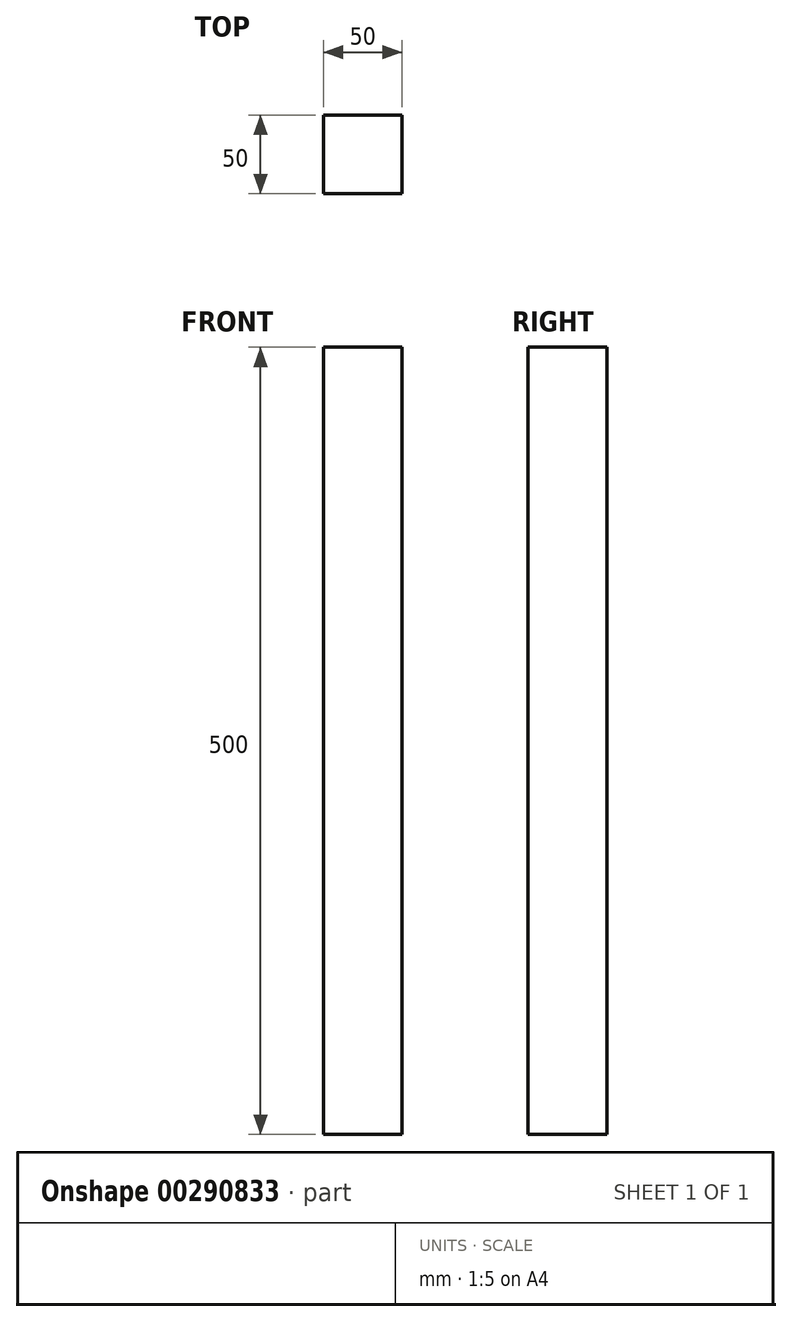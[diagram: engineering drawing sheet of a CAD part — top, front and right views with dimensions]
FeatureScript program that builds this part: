
annotation { "Feature Type Name" : "Feature", "Feature Type Description" : "" }
export const myFeature = defineFeature(function(context is Context, id is Id, definition is map)
    precondition{}
    {
        {
            var Q0;
            Q0=qCreatedBy(makeId("Top.planeOp"),FACE);
            var sketch = newSketch(context, id + "F0", { "sketchPlane" : qUnion([Q0])});
            skLineSegment(sketch, "E0.bottom", {"start": v(25, -25) * mm, "end": v(-25, -25) * mm});
            skLineSegment(sketch, "E0.top", {"start": v(25, 25) * mm, "end": v(-25, 25) * mm});
            skLineSegment(sketch, "E0.left", {"start": v(25, -25) * mm, "end": v(25, 25) * mm});
            skLineSegment(sketch, "E0.right", {"start": v(-25, -25) * mm, "end": v(-25, 25) * mm});
            skPoint(sketch, "E0.middle", {"position": v(0, 0) * mm});
            skSolve(sketch);
        }
        {
            var Q0;
            Q0=makeQuery(id+"F0.imprint","IMPRINT",FACE,{"disambiguationData":[TD([[makeQuery(id+"F0.imprint","IMPRINT",EDGE,{"derivedFrom":sQuery(id+"F0.wireOp",EDGE,"E0.bottom")}),-1.0]])]});
            extrude(context, id + "F1", {"entities" : qUnion([Q0]), "depth" : 500 * mm});
        }
    });
